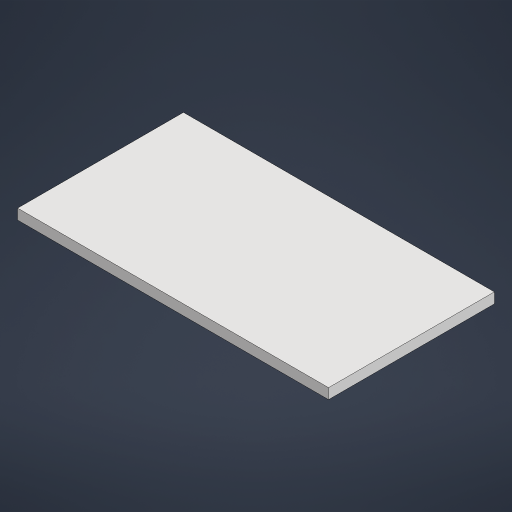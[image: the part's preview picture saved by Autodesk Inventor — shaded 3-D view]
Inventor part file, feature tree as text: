
AUTODESK INVENTOR PART (.ipt)
format: ipt  version: 2023.1 (Build 271208000, 208)  size: 152,064 bytes
history: native  units: in
note: dims shown in document units (in); Inventor stores cm internally (conversion verified against a paired STEP export)
features: extrude x1, sketch x1
ambient origin geometry x8: Origin, YZ Plane, XZ Plane, XY Plane, X Axis, Y Axis, Z Axis, Center Point
bodies: Solid1 (feature_tree)
feature tree (2):
  extrude  "Extrusion1"  Depth=16.0in
  sketch  "Sketch2"  dims[d3=30.0in d4=16.0in d5=1.0in d6=0.0in]
